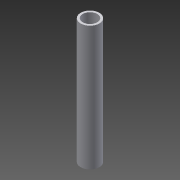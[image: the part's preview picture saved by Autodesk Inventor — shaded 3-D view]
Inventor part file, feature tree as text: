
AUTODESK INVENTOR PART (.ipt)
format: ipt  version: 2015 (Build 190159000, 159)  size: 87,552 bytes
history: native  units: mm
features: other x2, extrude x1, shell x1, sketch x1
ambient origin geometry x8: Origin, YZ Plane, XZ Plane, XY Plane, X Axis, Y Axis, Z Axis, Center Point
bodies: Body1 (feature_tree)
feature tree (5):
  other  "Bryła1"
  other  "Płaszczyzna konstrukcyjna1"
  extrude  "Wyciągnięcie proste1"  [1 undecoded]
  shell  "Skorupa2"  Thickness=18.0mm
  sketch  "Szkic1"
note: 1 required parameter value undecoded (feature->parameter linkage not recoverable at this tier; creation-order binding heuristic only, values carry confidence <= 0.55)
